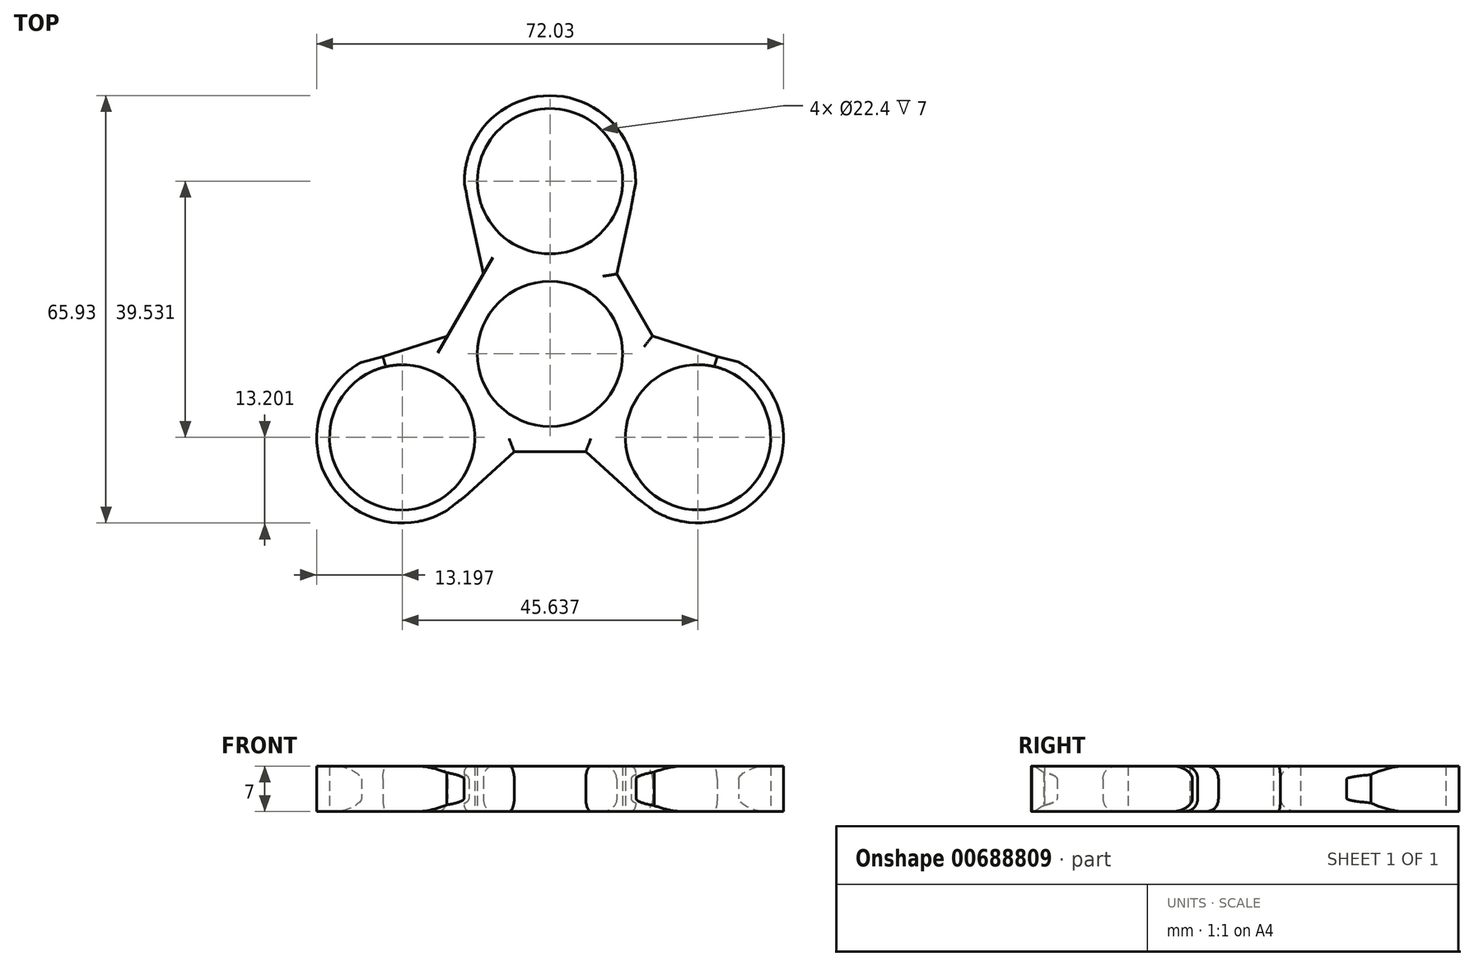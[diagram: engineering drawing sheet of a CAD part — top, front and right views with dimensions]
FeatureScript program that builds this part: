
annotation { "Feature Type Name" : "Feature", "Feature Type Description" : "" }
export const myFeature = defineFeature(function(context is Context, id is Id, definition is map)
    precondition{}
    {
        {
            var Q0;
            Q0=qCreatedBy(makeId("Top.planeOp"),FACE);
            var sketch = newSketch(context, id + "F0", { "sketchPlane" : qUnion([Q0])});
            skCircle(sketch, "E0", {"center": v(0, 0) * mm, "radius": 11.2 * mm});
            skCircle(sketch, "E1", {"center": v(0, 26.64) * mm, "radius": 11.2 * mm});
            skArc(sketch, "E2", {"start": v(13.2, 26.28) * mm, "mid": v(0, 39.84) * mm, "end": v(-13.2, 26.28) * mm});
            skArc(sketch, "E3.1.0", {"start": v(-29.1, -1.28) * mm, "mid": v(-34.24, -19.49) * mm, "end": v(-15.9, -24.14) * mm});
            skCircle(sketch, "E3.1.1", {"center": v(-22.8, -12.89) * mm, "radius": 11.2 * mm});
            skArc(sketch, "E3.2.0", {"start": v(16.06, -24.2) * mm, "mid": v(34.3, -19.4) * mm, "end": v(29.12, -1.27) * mm});
            skCircle(sketch, "E3.2.1", {"center": v(22.83, -12.87) * mm, "radius": 11.2 * mm});
            skPoint(sketch, "E3.center", {"position": v(0, 0.3) * mm});
            skArc(sketch, "E4", {"start": v(-12.5, 22.55) * mm, "mid": v(-12.84, 24.42) * mm, "end": v(-13.2, 26.28) * mm});
            skPoint(sketch, "E5.orphan", {"position": v(-10.3, -1.17) * mm});
            skPoint(sketch, "E6.orphan", {"position": v(10.3, -1.17) * mm});
            skPoint(sketch, "E7.orphan", {"position": v(-3.86, 9.93) * mm});
            skPoint(sketch, "E8.orphan", {"position": v(6.43, -7.9) * mm});
            skPoint(sketch, "E9.orphan", {"position": v(-6.4, -7.88) * mm});
            skLineSegment(sketch, "E10", {"start": v(-12.5, 22.55) * mm, "end": v(-10.3, 12.32) * mm});
            skLineSegment(sketch, "E11.1.0", {"start": v(-13.27, -22.1) * mm, "end": v(-5.52, -15.07) * mm});
            skLineSegment(sketch, "E11.2.0", {"start": v(25.78, -0.44) * mm, "end": v(15.82, 2.75) * mm});
            skLineSegment(sketch, "E12.MirrorCS", {"start": v(13.27, -22.1) * mm, "end": v(5.52, -15.07) * mm});
            skLineSegment(sketch, "E13.MirrorCS", {"start": v(-25.78, -0.44) * mm, "end": v(-15.82, 2.75) * mm});
            skLineSegment(sketch, "E14.MirrorCS", {"start": v(12.5, 22.55) * mm, "end": v(10.3, 12.32) * mm});
            skLineSegment(sketch, "E15", {"start": v(-10.3, 12.32) * mm, "end": v(-15.82, 2.75) * mm});
            skLineSegment(sketch, "E16.MirrorCS", {"start": v(10.3, 12.32) * mm, "end": v(15.82, 2.75) * mm});
            skLineSegment(sketch, "E17.1.0", {"start": v(-15.82, 2.75) * mm, "end": v(-10.3, 12.32) * mm});
            skLineSegment(sketch, "E17.2.0", {"start": v(5.52, -15.07) * mm, "end": v(-5.52, -15.07) * mm});
            skLineSegment(sketch, "E18", {"start": v(13.2, 26.28) * mm, "end": v(12.5, 22.55) * mm});
            skLineSegment(sketch, "E19", {"start": v(-29.1, -1.28) * mm, "end": v(-25.78, -0.44) * mm});
            skLineSegment(sketch, "E20", {"start": v(25.78, -0.44) * mm, "end": v(29.12, -1.27) * mm});
            skLineSegment(sketch, "E21", {"start": v(-13.27, -22.1) * mm, "end": v(-15.9, -24.14) * mm});
            skLineSegment(sketch, "E22", {"start": v(13.27, -22.1) * mm, "end": v(16.06, -24.2) * mm});
            skSolve(sketch);
        }
        {
            var Q0;
            Q0 = qSketchRegion(id + "F0", true);
            extrude(context, id + "F1", {"entities" : qUnion([Q0]), "depth" : 7 * mm, "offsetDistance" : 25 * mm});
        }
        {
            var Q0;
            Q0=makeQuery(id+"F1.opExtrude","CAP_EDGE",EDGE,{"disambiguationData":[OSD([sQuery(id+"F0.wireOp",EDGE,"E10")])],"isStart":false});
            var Q1;
            Q1=makeQuery(id+"F1.opExtrude","CAP_EDGE",EDGE,{"disambiguationData":[OSD([sQuery(id+"F0.wireOp",EDGE,"E17.1.0")])],"isStart":true});
            var Q2;
            Q2=makeQuery(id+"F1.opExtrude","CAP_EDGE",EDGE,{"disambiguationData":[OSD([sQuery(id+"F0.wireOp",EDGE,"E10")])],"isStart":true});
            var Q3;
            Q3=makeQuery(id+"F1.opExtrude","CAP_EDGE",EDGE,{"disambiguationData":[OSD([sQuery(id+"F0.wireOp",EDGE,"E17.1.0")])],"isStart":false});
            var Q4;
            Q4=makeQuery(id+"F1.opExtrude","CAP_EDGE",EDGE,{"disambiguationData":[OSD([sQuery(id+"F0.wireOp",EDGE,"E13.MirrorCS")])],"isStart":false});
            var Q5;
            Q5=makeQuery(id+"F1.opExtrude","CAP_EDGE",EDGE,{"disambiguationData":[OSD([sQuery(id+"F0.wireOp",EDGE,"E13.MirrorCS")])],"isStart":true});
            fillet(context, id + "F2", {"entities" : qUnion([Q0, Q1, Q2, Q3, Q4, Q5]), "radius" : 2 * mm, "tangentPropagation" : true, "allowEdgeOverflow" : false});
        }
        {
            var Q0;
            Q0=makeQuery(id+"F1.opExtrude","CAP_EDGE",EDGE,{"disambiguationData":[OSD([sQuery(id+"F0.wireOp",EDGE,"E14.MirrorCS")])],"isStart":true});
            var Q1;
            Q1=makeQuery(id+"F1.opExtrude","CAP_EDGE",EDGE,{"disambiguationData":[OSD([sQuery(id+"F0.wireOp",EDGE,"E16.MirrorCS")])],"isStart":false});
            var Q2;
            Q2=makeQuery(id+"F1.opExtrude","CAP_EDGE",EDGE,{"disambiguationData":[OSD([sQuery(id+"F0.wireOp",EDGE,"E14.MirrorCS")])],"isStart":false});
            var Q3;
            Q3=makeQuery(id+"F1.opExtrude","CAP_EDGE",EDGE,{"disambiguationData":[OSD([sQuery(id+"F0.wireOp",EDGE,"E16.MirrorCS")])],"isStart":true});
            var Q4;
            Q4=makeQuery(id+"F1.opExtrude","CAP_EDGE",EDGE,{"disambiguationData":[OSD([sQuery(id+"F0.wireOp",EDGE,"E11.2.0")])],"isStart":true});
            var Q5;
            Q5=makeQuery(id+"F1.opExtrude","CAP_EDGE",EDGE,{"disambiguationData":[OSD([sQuery(id+"F0.wireOp",EDGE,"E11.2.0")])],"isStart":false});
            fillet(context, id + "F3", {"entities" : qUnion([Q0, Q1, Q2, Q3, Q4, Q5]), "radius" : 2 * mm, "tangentPropagation" : true, "allowEdgeOverflow" : false});
        }
        {
            var Q0;
            Q0=makeQuery(id+"F1.opExtrude","CAP_EDGE",EDGE,{"disambiguationData":[OSD([sQuery(id+"F0.wireOp",EDGE,"E12.MirrorCS")])],"isStart":false});
            var Q1;
            Q1=makeQuery(id+"F1.opExtrude","CAP_EDGE",EDGE,{"disambiguationData":[OSD([sQuery(id+"F0.wireOp",EDGE,"E17.2.0")])],"isStart":false});
            var Q2;
            Q2=makeQuery(id+"F1.opExtrude","CAP_EDGE",EDGE,{"disambiguationData":[OSD([sQuery(id+"F0.wireOp",EDGE,"E17.2.0")])],"isStart":true});
            var Q3;
            Q3=makeQuery(id+"F1.opExtrude","CAP_EDGE",EDGE,{"disambiguationData":[OSD([sQuery(id+"F0.wireOp",EDGE,"E12.MirrorCS")])],"isStart":true});
            var Q4;
            Q4=makeQuery(id+"F1.opExtrude","CAP_EDGE",EDGE,{"disambiguationData":[OSD([sQuery(id+"F0.wireOp",EDGE,"E11.1.0")])],"isStart":false});
            var Q5;
            Q5=makeQuery(id+"F1.opExtrude","CAP_EDGE",EDGE,{"disambiguationData":[OSD([sQuery(id+"F0.wireOp",EDGE,"E11.1.0")])],"isStart":true});
            fillet(context, id + "F4", {"entities" : qUnion([Q0, Q1, Q2, Q3, Q4, Q5]), "radius" : 2 * mm, "tangentPropagation" : true, "allowEdgeOverflow" : false});
        }
    });
